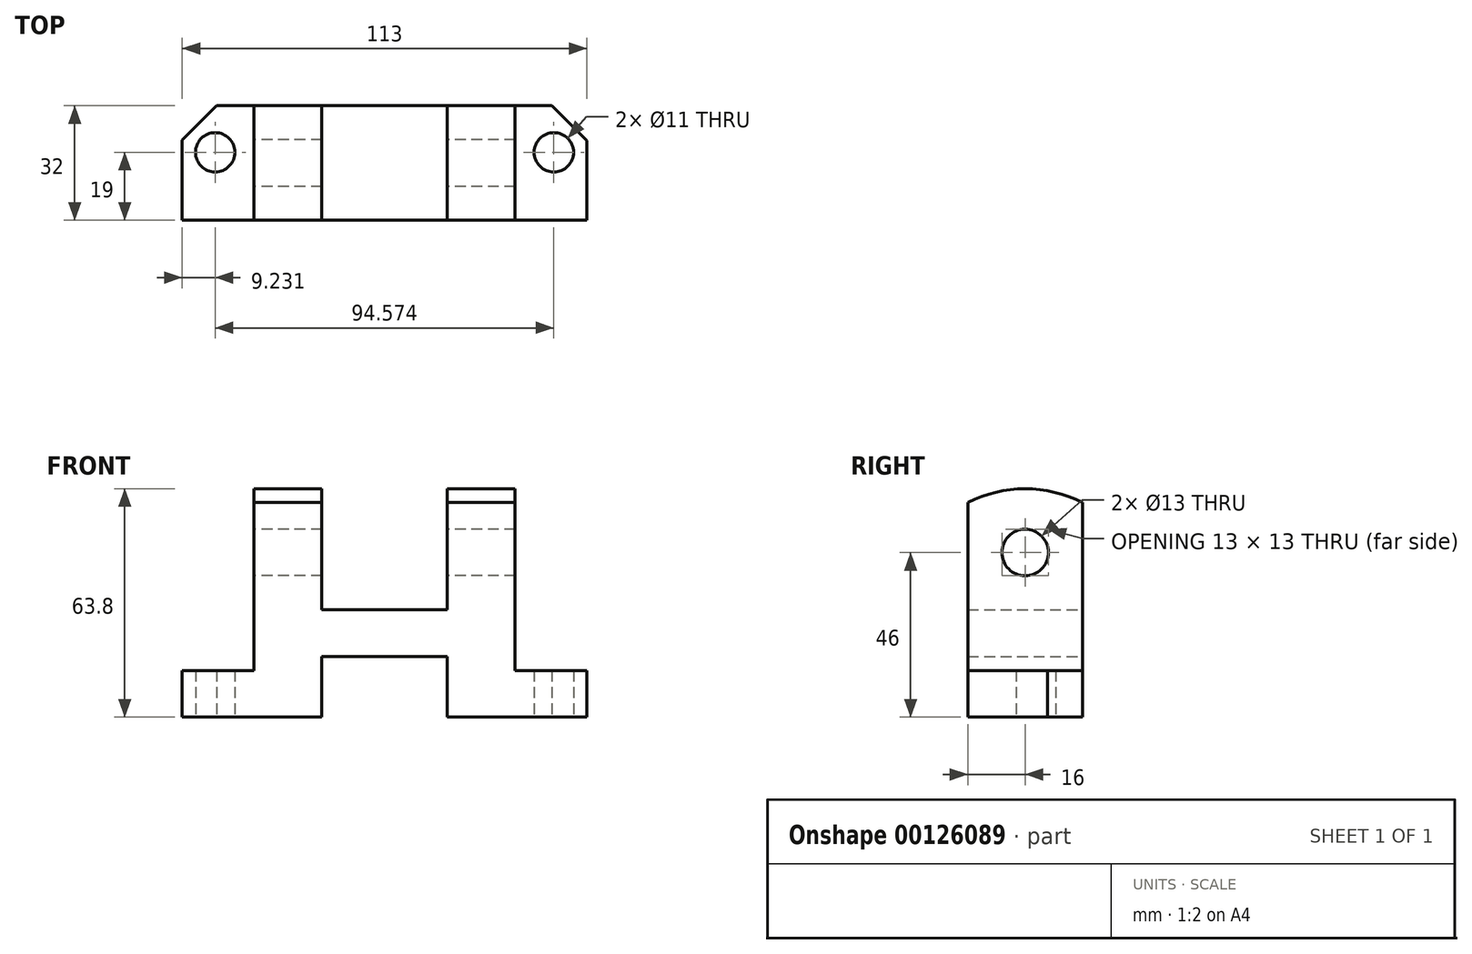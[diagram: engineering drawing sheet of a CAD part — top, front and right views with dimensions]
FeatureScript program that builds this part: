
annotation { "Feature Type Name" : "Feature", "Feature Type Description" : "" }
export const myFeature = defineFeature(function(context is Context, id is Id, definition is map)
    precondition{}
    {
        {
            var Q0;
            Q0=qCreatedBy(makeId("Front.planeOp"),FACE);
            var sketch = newSketch(context, id + "F0", { "sketchPlane" : qUnion([Q0])});
            skLineSegment(sketch, "E0", {"start": v(0, 0) * mm, "end": v(39, 0) * mm});
            skLineSegment(sketch, "E1", {"start": v(39, 0) * mm, "end": v(39, 17) * mm});
            skLineSegment(sketch, "E2", {"start": v(39, 17) * mm, "end": v(74, 17) * mm});
            skLineSegment(sketch, "E3", {"start": v(74, 17) * mm, "end": v(74, 0) * mm});
            skLineSegment(sketch, "E4", {"start": v(74, 0) * mm, "end": v(113, 0) * mm});
            skLineSegment(sketch, "E5", {"start": v(113, 0) * mm, "end": v(113, 13) * mm});
            skLineSegment(sketch, "E6", {"start": v(113, 13) * mm, "end": v(93, 13) * mm});
            skLineSegment(sketch, "E7", {"start": v(93, 13) * mm, "end": v(93, 64) * mm});
            skLineSegment(sketch, "E8", {"start": v(93, 64) * mm, "end": v(74, 64) * mm});
            skLineSegment(sketch, "E9", {"start": v(74, 64) * mm, "end": v(74, 30) * mm});
            skLineSegment(sketch, "E10", {"start": v(74, 30) * mm, "end": v(39, 30) * mm});
            skLineSegment(sketch, "E11", {"start": v(39, 30) * mm, "end": v(39, 64) * mm});
            skLineSegment(sketch, "E12", {"start": v(39, 64) * mm, "end": v(20, 64) * mm});
            skLineSegment(sketch, "E13", {"start": v(20, 64) * mm, "end": v(20, 13) * mm});
            skLineSegment(sketch, "E14", {"start": v(20, 13) * mm, "end": v(0, 13) * mm});
            skLineSegment(sketch, "E15", {"start": v(0, 13) * mm, "end": v(0, 0) * mm});
            skSolve(sketch);
        }
        {
            var Q0;
            Q0 = qSketchRegion(id + "F0", true);
            extrude(context, id + "F1", {"entities" : qUnion([Q0]), "depth" : 32 * mm});
        }
        {
            var Q0;
            Q0=qCreatedBy(makeId("Top.planeOp"),FACE);
            var sketch = newSketch(context, id + "F2", { "sketchPlane" : qUnion([Q0])});
            skCircle(sketch, "E16", {"center": v(9.23, -13) * mm, "radius": 5.5 * mm});
            skCircle(sketch, "E17", {"center": v(103.8, -13) * mm, "radius": 5.5 * mm});
            skLineSegment(sketch, "E18", {"start": v(0, 0) * mm, "end": v(0, -9.59) * mm});
            skLineSegment(sketch, "E19", {"start": v(0, -9.59) * mm, "end": v(9.59, 0) * mm});
            skLineSegment(sketch, "E20", {"start": v(9.59, 0) * mm, "end": v(0, 0) * mm});
            skLineSegment(sketch, "E21", {"start": v(113, 0) * mm, "end": v(103.24, 0) * mm});
            skLineSegment(sketch, "E22", {"start": v(103.24, 0) * mm, "end": v(113, -9.76) * mm});
            skLineSegment(sketch, "E23", {"start": v(113, -9.76) * mm, "end": v(113, 0) * mm});
            skSolve(sketch);
        }
        {
            var Q0;
            Q0 = qSketchRegion(id + "F2", true);
            extrude(context, id + "F3", {"entities" : qUnion([Q0]), "operationType" : NewBodyOperationType.REMOVE, "depth" : 25 * mm});
        }
        {
            var Q0;
            Q0=qCreatedBy(makeId("Right.planeOp"),FACE);
            var sketch = newSketch(context, id + "F4", { "sketchPlane" : qUnion([Q0])});
            skCircle(sketch, "E24", {"center": v(-16, 46) * mm, "radius": 6.5 * mm});
            skLineSegment(sketch, "E25", {"start": v(0, 59.93) * mm, "end": v(0, 64) * mm});
            skLineSegment(sketch, "E26", {"start": v(0, 64) * mm, "end": v(-32, 64) * mm});
            skLineSegment(sketch, "E27", {"start": v(-32, 64) * mm, "end": v(-32, 59.93) * mm});
            skArc(sketch, "E28", {"start": v(0, 59.93) * mm, "mid": v(-16, 63.8) * mm, "end": v(-32, 59.93) * mm});
            skSolve(sketch);
        }
        {
            var Q0;
            Q0 = qSketchRegion(id + "F4", true);
            extrude(context, id + "F5", {"entities" : qUnion([Q0]), "operationType" : NewBodyOperationType.REMOVE, "endBound" : BoundingType.THROUGH_ALL, "depth" : 25 * mm});
        }
    });
